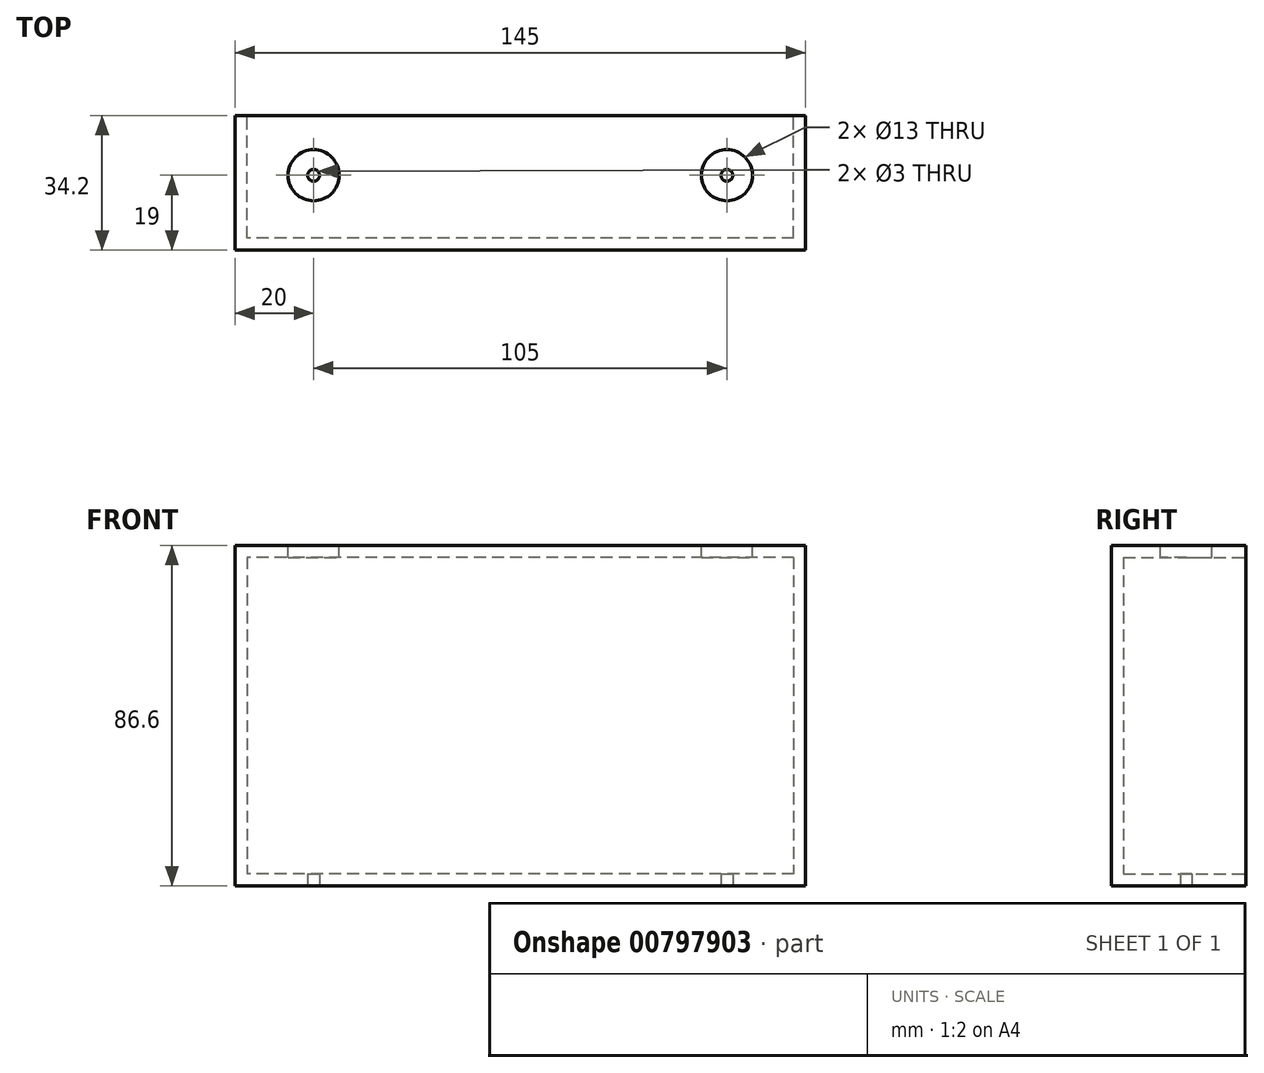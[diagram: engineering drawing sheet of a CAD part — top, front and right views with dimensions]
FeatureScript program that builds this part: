
annotation { "Feature Type Name" : "Feature", "Feature Type Description" : "" }
export const myFeature = defineFeature(function(context is Context, id is Id, definition is map)
    precondition{}
    {
        {
            var Q0;
            Q0=qCreatedBy(makeId("Front.planeOp"),FACE);
            var sketch = newSketch(context, id + "F0", { "sketchPlane" : qUnion([Q0])});
            skLineSegment(sketch, "E0.bottom", {"start": v(72.5, 43.3) * mm, "end": v(-72.5, 43.3) * mm});
            skLineSegment(sketch, "E0.top", {"start": v(72.5, -43.3) * mm, "end": v(-72.5, -43.3) * mm});
            skLineSegment(sketch, "E0.left", {"start": v(72.5, 43.3) * mm, "end": v(72.5, -43.3) * mm});
            skLineSegment(sketch, "E0.right", {"start": v(-72.5, 43.3) * mm, "end": v(-72.5, -43.3) * mm});
            skPoint(sketch, "E0.middle", {"position": v(0, 0) * mm});
            skLineSegment(sketch, "E1.bottom", {"start": v(69.45, 40.25) * mm, "end": v(-69.45, 40.25) * mm});
            skLineSegment(sketch, "E1.top", {"start": v(69.45, -40.25) * mm, "end": v(-69.45, -40.25) * mm});
            skLineSegment(sketch, "E1.left", {"start": v(69.45, 40.25) * mm, "end": v(69.45, -40.25) * mm});
            skLineSegment(sketch, "E1.right", {"start": v(-69.45, 40.25) * mm, "end": v(-69.45, -40.25) * mm});
            skSolve(sketch);
        }
        {
            var Q0;
            Q0=qSketchRegion(id+"F0",true);
            extrude(context, id + "F1", {"entities" : qUnion([Q0]), "depth" : 31.15 * mm, "offsetDistance" : 25 * mm});
        }
        {
            var Q0;
            Q0=makeQuery(id+"F1.opExtrude","CAP_FACE",FACE,{"disambiguationData":[OSD([sQuery(id+"F0.wireOp",EDGE,"E0.bottom"),sQuery(id+"F0.wireOp",EDGE,"E0.top"),sQuery(id+"F0.wireOp",EDGE,"E0.left"),sQuery(id+"F0.wireOp",EDGE,"E0.right"),sQuery(id+"F0.wireOp",EDGE,"E1.bottom"),sQuery(id+"F0.wireOp",EDGE,"E1.top"),sQuery(id+"F0.wireOp",EDGE,"E1.left"),sQuery(id+"F0.wireOp",EDGE,"E1.right")])],"isStart":false});
            var sketch = newSketch(context, id + "F2", { "sketchPlane" : qUnion([Q0])});
            skLineSegment(sketch, "E2.bottom", {"start": v(72.5, 43.3) * mm, "end": v(-72.5, 43.3) * mm});
            skLineSegment(sketch, "E2.top", {"start": v(72.5, -43.3) * mm, "end": v(-72.5, -43.3) * mm});
            skLineSegment(sketch, "E2.left", {"start": v(72.5, 43.3) * mm, "end": v(72.5, -43.3) * mm});
            skLineSegment(sketch, "E2.right", {"start": v(-72.5, 43.3) * mm, "end": v(-72.5, -43.3) * mm});
            skPoint(sketch, "E2.middle", {"position": v(0, 0) * mm});
            skSolve(sketch);
        }
        {
            var Q0;
            Q0=qSketchRegion(id+"F2",true);
            extrude(context, id + "F3", {"entities" : qUnion([Q0]), "operationType" : NewBodyOperationType.ADD, "depth" : 3.05 * mm, "offsetDistance" : 25 * mm});
        }
        {
            var Q0;
            Q0=makeQuery(id+"F3.boolean.opBoolean","MERGE",FACE,{"derivedFrom":[makeQuery(id+"F1.opExtrude","SWEPT_FACE",FACE,{"disambiguationData":[OSD([sQuery(id+"F0.wireOp",EDGE,"E0.bottom")])]}),makeQuery(id+"F3.opExtrude","SWEPT_FACE",FACE,{"disambiguationData":[OSD([sQuery(id+"F2.wireOp",EDGE,"E2.bottom")])]})]});
            var sketch = newSketch(context, id + "F4", { "sketchPlane" : qUnion([Q0])});
            skCircle(sketch, "E3", {"center": v(-52.5, -15.2) * mm, "radius": 6.5 * mm});
            skCircle(sketch, "E4", {"center": v(52.5, -15.2) * mm, "radius": 6.5 * mm});
            skLineSegment(sketch, "E5", {"start": v(-72.5, 0) * mm, "end": v(-72.5, -34.2) * mm, "construction": true});
            skLineSegment(sketch, "E6", {"start": v(52.5, -15.2) * mm, "end": v(-52.5, -15.2) * mm, "construction": true});
            skLineSegment(sketch, "E7", {"start": v(72.5, 0) * mm, "end": v(-72.5, 0) * mm, "construction": true});
            skSolve(sketch);
        }
        {
            var Q0;
            Q0=qSketchRegion(id+"F4",true);
            extrude(context, id + "F5", {"entities" : qUnion([Q0]), "operationType" : NewBodyOperationType.REMOVE, "oppositeDirection" : true, "depth" : 25 * mm, "offsetDistance" : 25 * mm});
        }
        {
            var Q0;
            Q0=makeQuery(id+"F3.boolean.opBoolean","MERGE",FACE,{"derivedFrom":[makeQuery(id+"F1.opExtrude","SWEPT_FACE",FACE,{"disambiguationData":[OSD([sQuery(id+"F0.wireOp",EDGE,"E0.top")])]}),makeQuery(id+"F3.opExtrude","SWEPT_FACE",FACE,{"disambiguationData":[OSD([sQuery(id+"F2.wireOp",EDGE,"E2.top")])]})]});
            var sketch = newSketch(context, id + "F6", { "sketchPlane" : qUnion([Q0])});
            skCircle(sketch, "E8", {"center": v(-52.5, 15.2) * mm, "radius": 1.5 * mm});
            skCircle(sketch, "E9", {"center": v(52.5, 15.2) * mm, "radius": 1.5 * mm});
            skSolve(sketch);
        }
        {
            var Q0;
            Q0=qSketchRegion(id+"F6",true);
            extrude(context, id + "F7", {"entities" : qUnion([Q0]), "operationType" : NewBodyOperationType.REMOVE, "oppositeDirection" : true, "depth" : 25 * mm, "offsetDistance" : 25 * mm});
        }
    });
